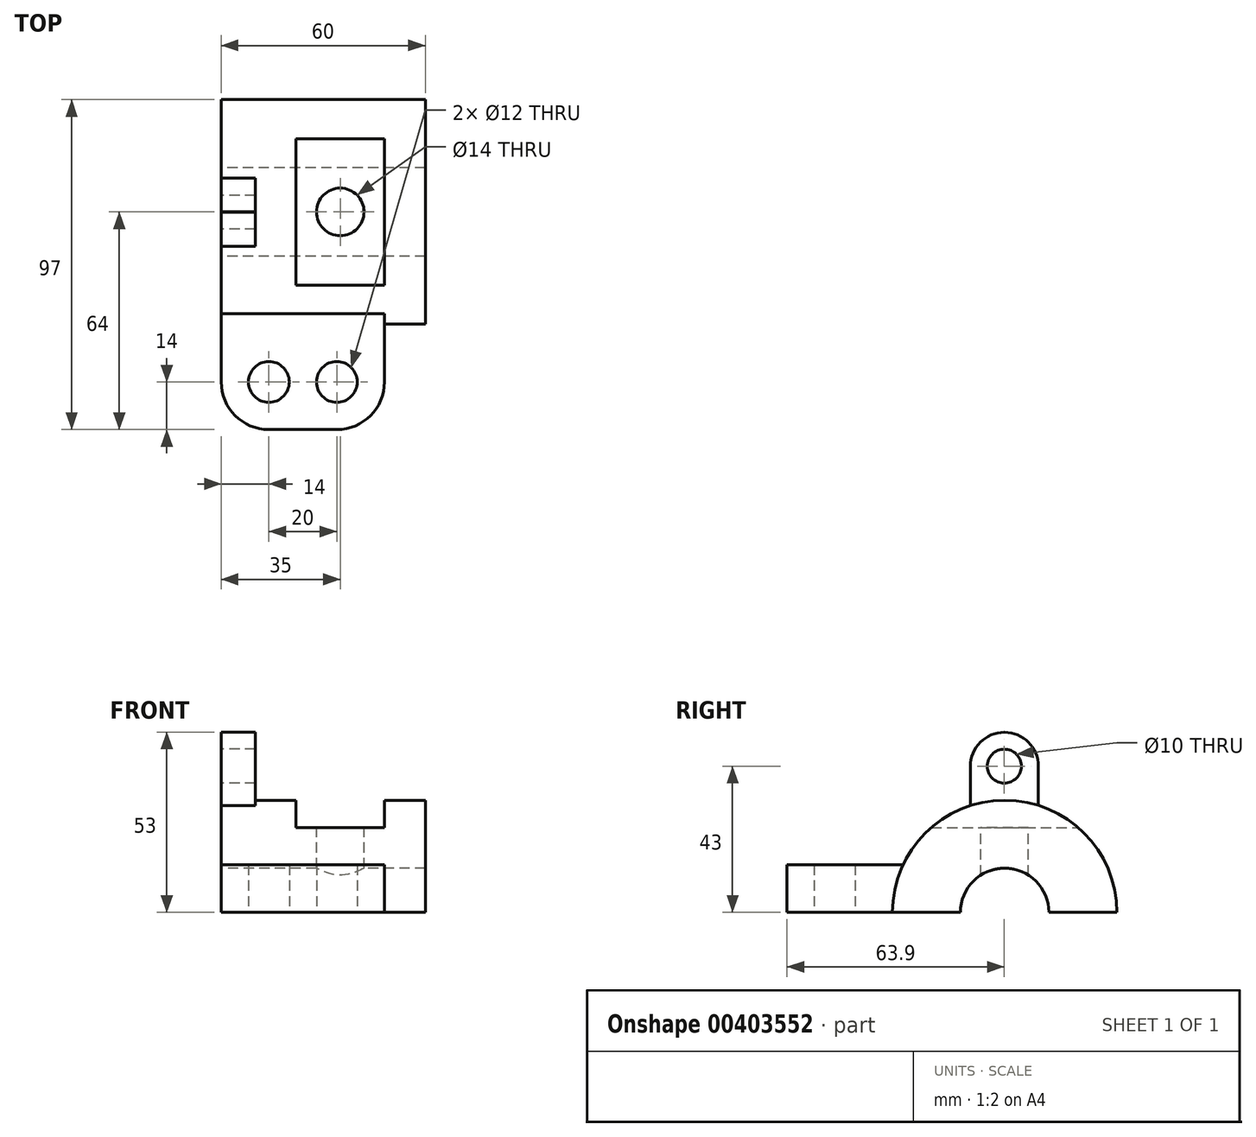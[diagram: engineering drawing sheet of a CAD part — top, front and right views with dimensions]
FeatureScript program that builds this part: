
annotation { "Feature Type Name" : "Feature", "Feature Type Description" : "" }
export const myFeature = defineFeature(function(context is Context, id is Id, definition is map)
    precondition{}
    {
        {
            var Q0;
            Q0=qCreatedBy(makeId("Right.planeOp"),FACE);
            var sketch = newSketch(context, id + "F0", { "sketchPlane" : qUnion([Q0])});
            skArc(sketch, "E0", {"start": v(33, 0) * mm, "mid": v(0, 33) * mm, "end": v(-33, 0) * mm});
            skArc(sketch, "E1", {"start": v(13, 0) * mm, "mid": v(0, 13) * mm, "end": v(-13, 0) * mm});
            skLineSegment(sketch, "E2.bottom", {"start": v(-33, 0) * mm, "end": v(-13, 0) * mm});
            skLineSegment(sketch, "E3.trimOffspring", {"start": v(13, 0) * mm, "end": v(34.55, 0) * mm});
            skSolve(sketch);
        }
        {
            var Q0;
            Q0 = qSketchRegion(id + "F0", true);
            extrude(context, id + "F1", {"entities" : qUnion([Q0]), "endBound" : BoundingType.SYMMETRIC, "depth" : 60 * mm});
        }
        {
            var Q0;
            Q0=makeQuery(id+"F1.opExtrude","SWEPT_FACE",FACE,{"disambiguationData":[OSD([sQuery(id+"F0.wireOp",EDGE,"E2.bottom")])]});
            var sketch = newSketch(context, id + "F2", { "sketchPlane" : qUnion([Q0])});
            skLineSegment(sketch, "E4", {"start": v(18, 33) * mm, "end": v(18, 50) * mm});
            skLineSegment(sketch, "E5", {"start": v(4, 64) * mm, "end": v(-16, 64) * mm});
            skLineSegment(sketch, "E6", {"start": v(-30, 50) * mm, "end": v(-30, 33) * mm});
            skPoint(sketch, "E7.visualSharp", {"position": v(-30, 64) * mm});
            skArc(sketch, "E7.filletArc", {"start": v(-16, 64) * mm, "mid": v(-25.9, 59.9) * mm, "end": v(-30, 50) * mm});
            skPoint(sketch, "E8.visualSharp", {"position": v(18, 64) * mm});
            skArc(sketch, "E8.filletArc", {"start": v(18, 50) * mm, "mid": v(13.9, 59.9) * mm, "end": v(4, 64) * mm});
            skCircle(sketch, "E9", {"center": v(-16, 50) * mm, "radius": 6 * mm});
            skCircle(sketch, "E10", {"center": v(4, 50) * mm, "radius": 6 * mm});
            skLineSegment(sketch, "E11", {"start": v(-30, 33) * mm, "end": v(-30, 28.1) * mm});
            skLineSegment(sketch, "E12", {"start": v(-30, 28.1) * mm, "end": v(18, 28.1) * mm});
            skLineSegment(sketch, "E13", {"start": v(18, 28.1) * mm, "end": v(18, 33) * mm});
            skSolve(sketch);
        }
        {
            var Q0;
            Q0 = qSketchRegion(id + "F2", true);
            extrude(context, id + "F3", {"entities" : qUnion([Q0]), "operationType" : NewBodyOperationType.ADD, "oppositeDirection" : true, "depth" : 14 * mm});
        }
        {
            var Q0;
            Q0=makeQuery(id+"F3.boolean.opBoolean","MERGE",FACE,{"derivedFrom":[makeQuery(id+"F1.opExtrude","CAP_FACE",FACE,{"disambiguationData":[OSD([sQuery(id+"F0.wireOp",EDGE,"E0"),sQuery(id+"F0.wireOp",EDGE,"E1"),sQuery(id+"F0.wireOp",EDGE,"E2.bottom"),sQuery(id+"F0.wireOp",EDGE,"E3.trimOffspring")])],"isStart":true}),makeQuery(id+"F3.opExtrude","SWEPT_FACE",FACE,{"disambiguationData":[OSD([sQuery(id+"F2.wireOp",EDGE,"E6"),sQuery(id+"F2.wireOp",EDGE,"E11")])]})]});
            var sketch = newSketch(context, id + "F4", { "sketchPlane" : qUnion([Q0])});
            skLineSegment(sketch, "E14.bottom", {"start": v(0, 53) * mm, "end": v(0.1, 53) * mm});
            skLineSegment(sketch, "E14.left", {"start": v(-9.9, 43) * mm, "end": v(-9.9, 30.95) * mm});
            skLineSegment(sketch, "E14.right", {"start": v(10.1, 42.9) * mm, "end": v(10.1, 30.95) * mm});
            skPoint(sketch, "E15.visualSharp", {"position": v(-9.9, 53) * mm});
            skArc(sketch, "E15.filletArc", {"start": v(0.1, 53) * mm, "mid": v(-6.97, 50.07) * mm, "end": v(-9.9, 43) * mm});
            skPoint(sketch, "E16.visualSharp", {"position": v(10.1, 53) * mm});
            skArc(sketch, "E16.filletArc", {"start": v(10.1, 42.9) * mm, "mid": v(7.14, 50.04) * mm, "end": v(0, 53) * mm});
            skLineSegment(sketch, "E17", {"start": v(-9.9, 30.95) * mm, "end": v(10.1, 30.95) * mm});
            skCircle(sketch, "E18", {"center": v(0.1, 43) * mm, "radius": 5 * mm});
            skSolve(sketch);
        }
        {
            var Q0;
            Q0 = qSketchRegion(id + "F4", true);
            extrude(context, id + "F5", {"entities" : qUnion([Q0]), "operationType" : NewBodyOperationType.ADD, "oppositeDirection" : true, "depth" : 10 * mm});
        }
        {
            var Q0;
            Q0=makeQuery(id+"F3.boolean.opBoolean","MERGE",FACE,{"derivedFrom":[makeQuery(id+"F1.opExtrude","SWEPT_FACE",FACE,{"disambiguationData":[OSD([sQuery(id+"F0.wireOp",EDGE,"E2.bottom")])]}),makeQuery(id+"F3.opExtrude","CAP_FACE",FACE,{"disambiguationData":[OSD([sQuery(id+"F2.wireOp",EDGE,"E4"),sQuery(id+"F2.wireOp",EDGE,"E5"),sQuery(id+"F2.wireOp",EDGE,"E6"),sQuery(id+"F2.wireOp",EDGE,"E7.filletArc"),sQuery(id+"F2.wireOp",EDGE,"E8.filletArc"),sQuery(id+"F2.wireOp",EDGE,"E9"),sQuery(id+"F2.wireOp",EDGE,"E10"),sQuery(id+"F2.wireOp",EDGE,"E11"),sQuery(id+"F2.wireOp",EDGE,"E12"),sQuery(id+"F2.wireOp",EDGE,"E13")])],"isStart":true})]});
            cPlane(context, id + "F6", {"entities" : qUnion([Q0]), "cplaneType" : CPlaneType.OFFSET, "offset" : 33 * mm, "oppositeDirection" : true, "width" : 150 * mm, "height" : 150 * mm});
        }
        {
            var Q0;
            Q0=qCreatedBy(id+"F6.planeOp",FACE);
            var sketch = newSketch(context, id + "F7", { "sketchPlane" : qUnion([Q0])});
            skLineSegment(sketch, "E19.bottom", {"start": v(-8, 33) * mm, "end": v(18, 33) * mm});
            skLineSegment(sketch, "E19.top", {"start": v(-8, -33) * mm, "end": v(18, -33) * mm});
            skLineSegment(sketch, "E19.left", {"start": v(-8, 33) * mm, "end": v(-8, -33) * mm});
            skLineSegment(sketch, "E19.right", {"start": v(18, 33) * mm, "end": v(18, -33) * mm});
            skSolve(sketch);
        }
        {
            var Q0;
            Q0 = qSketchRegion(id + "F7", true);
            extrude(context, id + "F8", {"entities" : qUnion([Q0]), "operationType" : NewBodyOperationType.REMOVE, "depth" : 8 * mm});
        }
        {
            var Q0;
            Q0=makeQuery(id+"F8.boolean.opBoolean","COPY",FACE,{"derivedFrom":makeQuery(id+"F8.opExtrude","CAP_FACE",FACE,{"disambiguationData":[OSD([sQuery(id+"F7.wireOp",EDGE,"E19.bottom"),sQuery(id+"F7.wireOp",EDGE,"E19.top"),sQuery(id+"F7.wireOp",EDGE,"E19.left"),sQuery(id+"F7.wireOp",EDGE,"E19.right")])],"isStart":false})});
            var sketch = newSketch(context, id + "F9", { "sketchPlane" : qUnion([Q0])});
            skCircle(sketch, "E20", {"center": v(5, 0) * mm, "radius": 7 * mm});
            skSolve(sketch);
        }
        {
            var Q0;
            Q0 = qSketchRegion(id + "F9", true);
            extrude(context, id + "F10", {"entities" : qUnion([Q0]), "operationType" : NewBodyOperationType.REMOVE, "endBound" : BoundingType.THROUGH_ALL, "oppositeDirection" : true, "depth" : 25 * mm});
        }
    });
